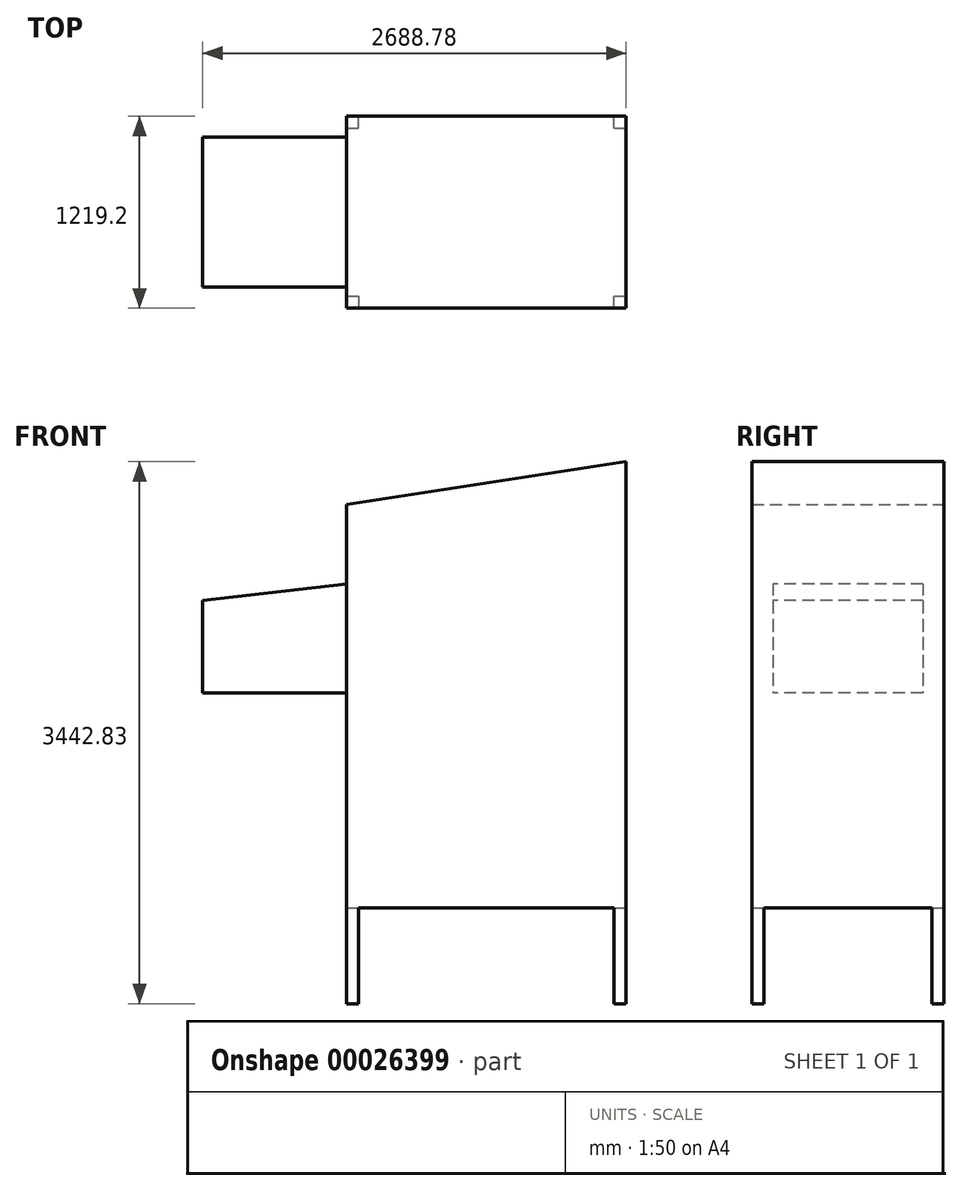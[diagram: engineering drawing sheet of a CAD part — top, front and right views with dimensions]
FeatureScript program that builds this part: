
annotation { "Feature Type Name" : "Feature", "Feature Type Description" : "" }
export const myFeature = defineFeature(function(context is Context, id is Id, definition is map)
    precondition{}
    {
        {
            var Q0;
            Q0=qCreatedBy(makeId("Front.planeOp"),FACE);
            var sketch = newSketch(context, id + "F0", { "sketchPlane" : qUnion([Q0])});
            skLineSegment(sketch, "E0.top", {"start": v(-516.76, -300.93) * mm, "end": v(1257.62, -300.93) * mm});
            skLineSegment(sketch, "E0.left", {"start": v(-516.76, 2259.39) * mm, "end": v(-516.76, -300.93) * mm});
            skLineSegment(sketch, "E1.top", {"start": v(-516.76, -910.53) * mm, "end": v(-440.56, -910.53) * mm});
            skLineSegment(sketch, "E1.left", {"start": v(-516.76, -300.93) * mm, "end": v(-516.76, -910.53) * mm});
            skLineSegment(sketch, "E2.top", {"start": v(1257.62, -910.53) * mm, "end": v(1181.42, -910.53) * mm});
            skLineSegment(sketch, "E2.left", {"start": v(1257.62, -300.93) * mm, "end": v(1257.62, -910.53) * mm});
            skLineSegment(sketch, "E3", {"start": v(1257.62, -300.93) * mm, "end": v(1257.62, 2532.3) * mm});
            skLineSegment(sketch, "E4", {"start": v(1257.62, 2532.3) * mm, "end": v(-516.76, 2259.39) * mm});
            skLineSegment(sketch, "E5", {"start": v(-440.56, -910.53) * mm, "end": v(-440.56, -300.93) * mm});
            skLineSegment(sketch, "E6", {"start": v(1181.42, -910.53) * mm, "end": v(1181.42, -300.93) * mm});
            skSolve(sketch);
        }
        {
            var Q0;
            {var subQ1=sQuery(id+"F0.wireOp",EDGE,"E0.left");Q0=makeQuery(id+"F0.imprint","IMPRINT",FACE,{"disambiguationData":[TD([[makeQuery(id+"F0.imprint","IMPRINT",EDGE,{"derivedFrom":subQ1}),1.0]])]});}
            extrude(context, id + "F1", {"entities" : qUnion([Q0]), "depth" : 1219.2 * mm});
        }
        {
            var Q0;
            Q0=makeQuery(id+"F0.imprint","IMPRINT",FACE,{"disambiguationData":[TD([[makeQuery(id+"F0.imprint","IMPRINT",EDGE,{"derivedFrom":sQuery(id+"F0.wireOp",EDGE,"E2.top")}),-1.0]])]});
            extrude(context, id + "F2", {"entities" : qUnion([Q0]), "operationType" : NewBodyOperationType.ADD, "depth" : 76.2 * mm});
        }
        {
            var Q0;
            Q0=makeQuery(id+"F1.opExtrude","SWEPT_FACE",FACE,{"disambiguationData":[OSD([sQuery(id+"F0.wireOp",EDGE,"E0.top")])]});
            var sketch = newSketch(context, id + "F3", { "sketchPlane" : qUnion([Q0])});
            skLineSegment(sketch, "E7", {"start": v(-516.76, 1219.2) * mm, "end": v(-516.76, 1143) * mm});
            skLineSegment(sketch, "E8", {"start": v(-516.76, 1143) * mm, "end": v(-440.56, 1143) * mm});
            skLineSegment(sketch, "E9", {"start": v(-440.56, 1143) * mm, "end": v(-440.56, 1219.2) * mm});
            skLineSegment(sketch, "E10", {"start": v(-440.56, 1219.2) * mm, "end": v(-516.76, 1219.2) * mm});
            skLineSegment(sketch, "E11", {"start": v(1257.62, 1219.2) * mm, "end": v(1181.42, 1219.2) * mm});
            skLineSegment(sketch, "E12", {"start": v(1181.42, 1219.2) * mm, "end": v(1181.42, 1143) * mm});
            skLineSegment(sketch, "E13", {"start": v(1181.42, 1143) * mm, "end": v(1257.62, 1143) * mm});
            skLineSegment(sketch, "E14", {"start": v(1257.62, 1143) * mm, "end": v(1257.62, 1219.2) * mm});
            skSolve(sketch);
        }
        {
            var Q0;
            Q0=makeQuery(id+"F0.imprint","IMPRINT",FACE,{"disambiguationData":[TD([[makeQuery(id+"F0.imprint","IMPRINT",EDGE,{"derivedFrom":sQuery(id+"F0.wireOp",EDGE,"E1.top")}),1.0]])]});
            extrude(context, id + "F4", {"entities" : qUnion([Q0]), "operationType" : NewBodyOperationType.ADD, "depth" : 76.2 * mm});
        }
        {
            var Q0;
            Q0=makeQuery(id+"F3.imprint","IMPRINT",FACE,{"disambiguationData":[TD([[makeQuery(id+"F3.imprint","IMPRINT",EDGE,{"derivedFrom":sQuery(id+"F3.wireOp",EDGE,"E7")}),1.0]])]});
            extrude(context, id + "F5", {"entities" : qUnion([Q0]), "operationType" : NewBodyOperationType.ADD, "depth" : 609.6 * mm});
        }
        {
            var Q0;
            Q0=makeQuery(id+"F3.imprint","IMPRINT",FACE,{"disambiguationData":[TD([[makeQuery(id+"F3.imprint","IMPRINT",EDGE,{"derivedFrom":sQuery(id+"F3.wireOp",EDGE,"E11")}),-1.0]])]});
            extrude(context, id + "F6", {"entities" : qUnion([Q0]), "operationType" : NewBodyOperationType.ADD, "depth" : 609.6 * mm});
        }
        {
            var Q0;
            Q0=makeQuery(id+"F5.boolean.opBoolean","MERGE",FACE,{"derivedFrom":[makeQuery(id+"F4.boolean.opBoolean","MERGE",FACE,{"derivedFrom":[makeQuery(id+"F1.opExtrude","SWEPT_FACE",FACE,{"disambiguationData":[OSD([sQuery(id+"F0.wireOp",EDGE,"E0.left")])]}),makeQuery(id+"F4.opExtrude","SWEPT_FACE",FACE,{"disambiguationData":[OSD([sQuery(id+"F0.wireOp",EDGE,"E1.left")])]})]}),makeQuery(id+"F5.opExtrude","SWEPT_FACE",FACE,{"disambiguationData":[OSD([sQuery(id+"F3.wireOp",EDGE,"E7")])]})]});
            var sketch = newSketch(context, id + "F7", { "sketchPlane" : qUnion([Q0])});
            skLineSegment(sketch, "E15.bottom", {"start": v(133.93, 1756.7) * mm, "end": v(1085.27, 1756.7) * mm});
            skLineSegment(sketch, "E15.top", {"start": v(133.93, 1063.33) * mm, "end": v(1085.27, 1063.33) * mm});
            skLineSegment(sketch, "E15.left", {"start": v(133.93, 1756.7) * mm, "end": v(133.93, 1063.33) * mm});
            skLineSegment(sketch, "E15.right", {"start": v(1085.27, 1756.7) * mm, "end": v(1085.27, 1063.33) * mm});
            skSolve(sketch);
        }
        {
            var Q0;
            Q0=makeQuery(id+"F7.imprint","IMPRINT",FACE,{"disambiguationData":[TD([[makeQuery(id+"F7.imprint","IMPRINT",EDGE,{"derivedFrom":sQuery(id+"F7.wireOp",EDGE,"E15.bottom")}),-1.0]])]});
            extrude(context, id + "F8", {"entities" : qUnion([Q0]), "operationType" : NewBodyOperationType.ADD, "depth" : 914.4 * mm});
        }
        {
            var Q0;
            Q0=makeQuery(id+"F8.opExtrude","SWEPT_FACE",FACE,{"disambiguationData":[OSD([sQuery(id+"F7.wireOp",EDGE,"E15.right")])]});
            var sketch = newSketch(context, id + "F9", { "sketchPlane" : qUnion([Q0])});
            skLineSegment(sketch, "E16", {"start": v(-516.76, 1756.7) * mm, "end": v(-1431.16, 1649) * mm});
            skLineSegment(sketch, "E17", {"start": v(-1431.16, 1649) * mm, "end": v(-1431.16, 1756.7) * mm});
            skLineSegment(sketch, "E18", {"start": v(-1431.16, 1756.7) * mm, "end": v(-516.76, 1756.7) * mm});
            skSolve(sketch);
        }
        {
            var Q0;
            Q0=makeQuery(id+"F9.imprint","IMPRINT",FACE,{"disambiguationData":[TD([[makeQuery(id+"F9.imprint","IMPRINT",EDGE,{"derivedFrom":sQuery(id+"F9.wireOp",EDGE,"E16")}),-1.0]])]});
            extrude(context, id + "F10", {"entities" : qUnion([Q0]), "operationType" : NewBodyOperationType.REMOVE, "oppositeDirection" : true, "depth" : 2133.6 * mm});
        }
    });
